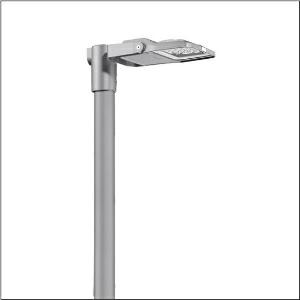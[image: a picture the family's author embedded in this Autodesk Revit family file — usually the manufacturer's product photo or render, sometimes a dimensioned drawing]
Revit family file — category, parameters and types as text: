
# Revit family: floodlight_fl_21_iq_micro___pl52_5xa7762a2d3a_f78f
name_source: partatom
category: Lighting Fixtures
units: mm (PartAtom-declared; Revit-internal decimal feet)

## family parameters
Cut with Voids When Loaded = No
Host = Face
Light Source = No
Part Type = Normal
Room Calculation Point = No
Round Connector Dimension = Use Diameter
Shared = No

## types (1)
- --- (1 x LED, 2890 lm, 23.1 W, 3000K)
    Apparent Load = 23 VA
    CIE Flux Codes = 26 60 98 100 100
    Color Rendering = 70
    Color Temperature = 3000K
    Default Elevation = 1800 mm
    Description = Floodlight FL 21 iQ micro, floodlight, primary light control with lens, of PMMA, primary optical cover: protective disc, of toughened safety glass, transparent, light distribution: PL52, light emission: direct distribution, installation type: surface-mounted, lamps: LED, High Power LED, rated values: 2.890lm | 23,1W | 125,1lm/W (begin service life); end service life: 2.890lm | 23,8W; at 50% lumin. flux: 1.445lm | 11W | 131,4lm/W, colour temperature: 3000K, colour rendering: CRI > 70, light colour: 730, light setting 1 begin service life: 100% | 2.890lm | 23,1W | 125,1lm/W | 3.000K, light setting 1 end service life: 23,8W, further light settings possible, control: Auto-Match, Temp-Guard, Night-Set, Smart-Wire, Desk-Remote (wireless, voltage-free reading and setting of iQ features in the workshop via application-optimized NFC function/RFID function), optimised constant luminous flux control (CLO 2.0), Street-Remote, pre-setting: linear dimming characteristic, with terminal, 6-pole, mains connection: 220..240V, AC, 50/60Hz, luminaire housing, of diecast aluminium, powder-coated, SITECO metallic grey (DB 702S), corrosivity category C5 mid according to DIN EN ISO 12944suitable for swimming poolschlorine-resistant, sealing non-destructively replaceable, please order mast flange separately, mast bracket, of steel, galvanised, powder-coated, SITECO metallic grey (DB 702S), protection rating (complete): IP66, insulation class (complete): insulation class II (safety insulation), certification: CE, ENEC, VDE, protection symbol: D, impact resistance: IK07, permissible operating ambient temperature: -40..+40°C, permissible operating ambient temperature for outdoor applications: -40..+50°C, standard: DIN EN 12944, LABS conformity tested according to VDMA 24364:2018-05, packaging unit: 1 piece

Light Distribution: PL52
    Height = 65 mm
    Lamp = 1 x LED
    Lamp Light Flux = 2890 lm
    Lamp Power = 23.1 W
    Lamp count = 1
    Length = 312 mm
    Luminous efficacy = 125 lm/W
    Manufacturer = Siteco
    ModVariant = No
    Model = 5XA7762A2D3A
    Mounting Place = Pole
    Mounting Type = Pole annexe
    Number of Poles = 1
    OnlyDefault = Yes
    Power Factor = 1
    Product Name = Floodlight FL 21 iQ micro | PL52
    Product group = floodlight | pylon annexe
    ProductGroupID = 6201
    Protection Class = Protection class II
    Protection Degree = IP 66
    RLX_Detail_Level = 1
    RLX_Emergency_Light_Flux = 0 lm
    RLX_Emergency_Type = 0
    RLX_Emergency_Type_DB = No
    RlxData = <blob elided: 102129 chars, md5=d1d6b50c>
    Socket = socket
    Standby Power = 0 W
    System Light Flux = 2890 lm
    System Power = 23 W
    Type Comments = factory setting: luminous flux: 100 % | dim-lin: 254 | 455 mA
    Type Image = l_1007121.jpg
    URL = http://relux.com
    VarID = @adj_178883
    Voltage = 0 V
    Weight = 0.00 kg
    Width = 230 mm

## geometry (parser evidence)
native form markers: Blend x4, Sweep x12
no freeform markers — native parametric forms only
